# Revit family: Stropný panel KINBETO_SPK
name_source: partatom
category: Obecné modely
units: mm (PartAtom-declared; Revit-internal decimal feet)

## family parameters
Bod výpočtu místnosti = Ne
Kóta kulaté spojky = Použít průměr
Může být hostitelem pro výztuž = Ne
Ořezat dutým tvarem při načtení = Ano
Sdílené = Ne
Typ dílu = Normální
Vždy vertikální = Ano
Založené na pracovní rovině = Ne

## types (5) — shared parameters
Atyp_panel / otvor alebo uhol = Vytvor novú Rodinu pre typ s orezom
Komentáře k typům = Predpäté stropné panely
Materiál = Beton C50/60
Minimálne uloženie (mm) = 100
Požiarna odolnosť = REI45
SP500 = Ne
Trieda predpínacej výstuže = Y1860S7
Typ obrázku = <Žádné>
URL = https://www.prefasu.sk
Výrobca kontakt = PREFA invest, a.s., Podhradská cesta 2, 038 52 Sučany
Výrobce = PREFA Sučany
zero-valued in all types: Výchozí výška

## per-type parameters (varying)
| type | Hmotnosť stropného panelu | Index kročajovej nepriezvučnosti (dB) | Index vzduchovej nepriezvučnosti (dB) | Model | Popis | SP200 | SP265 | SP320 | SP400 | Tepelný odpor |
| SPK 200 | 277.00 kg/m² | 81 | 49 | SP200 | Vystužené pozdĺžnou predpínacou výstužou | Ano | Ne | Ne | Ne | 0.1600 (m²·K)/W |
| SPK 265 | 360.00 kg/m² | 79 | 54 | SP265 | Vystužené pozdĺžnou predpínacou výstužou. | Ne | Ano | Ne | Ne | 0.1800 (m²·K)/W |
| SPK 320 | 383.00 kg/m² | 79 | 53 | SP320 | Vystužené pozdĺžnou predpínacou výstužou | Ne | Ne | Ano | Ne | 0.2000 (m²·K)/W |
| SPK 400 | 434.00 kg/m² | 76 | 57 | SP400 | Vystužené pozdĺžnou predpínacou výstužou | Ne | Ne | Ne | Ano | 0.2900 (m²·K)/W |
| SPK 500 | 600.00 kg/m² | 71 | 62 | SP500 | Vystužené pozdĺžnou predpínacou výstužou | Ne | Ne | Ne | Ano | 0.2600 (m²·K)/W |

## geometry (parser evidence)
native form markers: Sweep x13
no freeform markers — native parametric forms only
